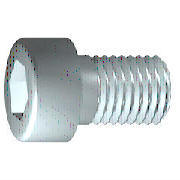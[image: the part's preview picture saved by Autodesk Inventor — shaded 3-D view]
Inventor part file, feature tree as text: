
AUTODESK INVENTOR PART (.ipt)
format: ipt  version: 2018 (Build 220112000, 112)  size: 195,072 bytes
history: native  units: mm (DEFAULTED — no unit token found)
features: sketch x2, extrude x1, plane x1, fillet x1
ambient origin geometry x7: Origin, YZ Plane, XY Plane, X Axis, Y Axis, Z Axis, Center Point
bodies: Solid1 (feature_tree), Body (feature_tree)
feature tree (5):
  extrude  "Slot"  Depth=6.0mm
  plane  "Work Plane1"
  fillet  "Fillet2"  Radius=6.0mm
  sketch  "Sketch1"  dims[d1=7.38655mm d2=0.61355mm d3=6.0mm]
  sketch  "Sketch2"  dims[d4=3.0mm d5=60.0deg d6=6.0mm d7=6.0mm d8=5.773503mm d9=10.0mm d10=90.0deg d11=10.0mm d12=0.0mm d13=7.38655mm d14=0.0mm d15=0.61345mm d16=0.61345mm d17=0.6mm d19=0.0mm d26=10.0mm d27=45.0deg d28=0.0mm d29=0.0mm d30=0.1mm]
